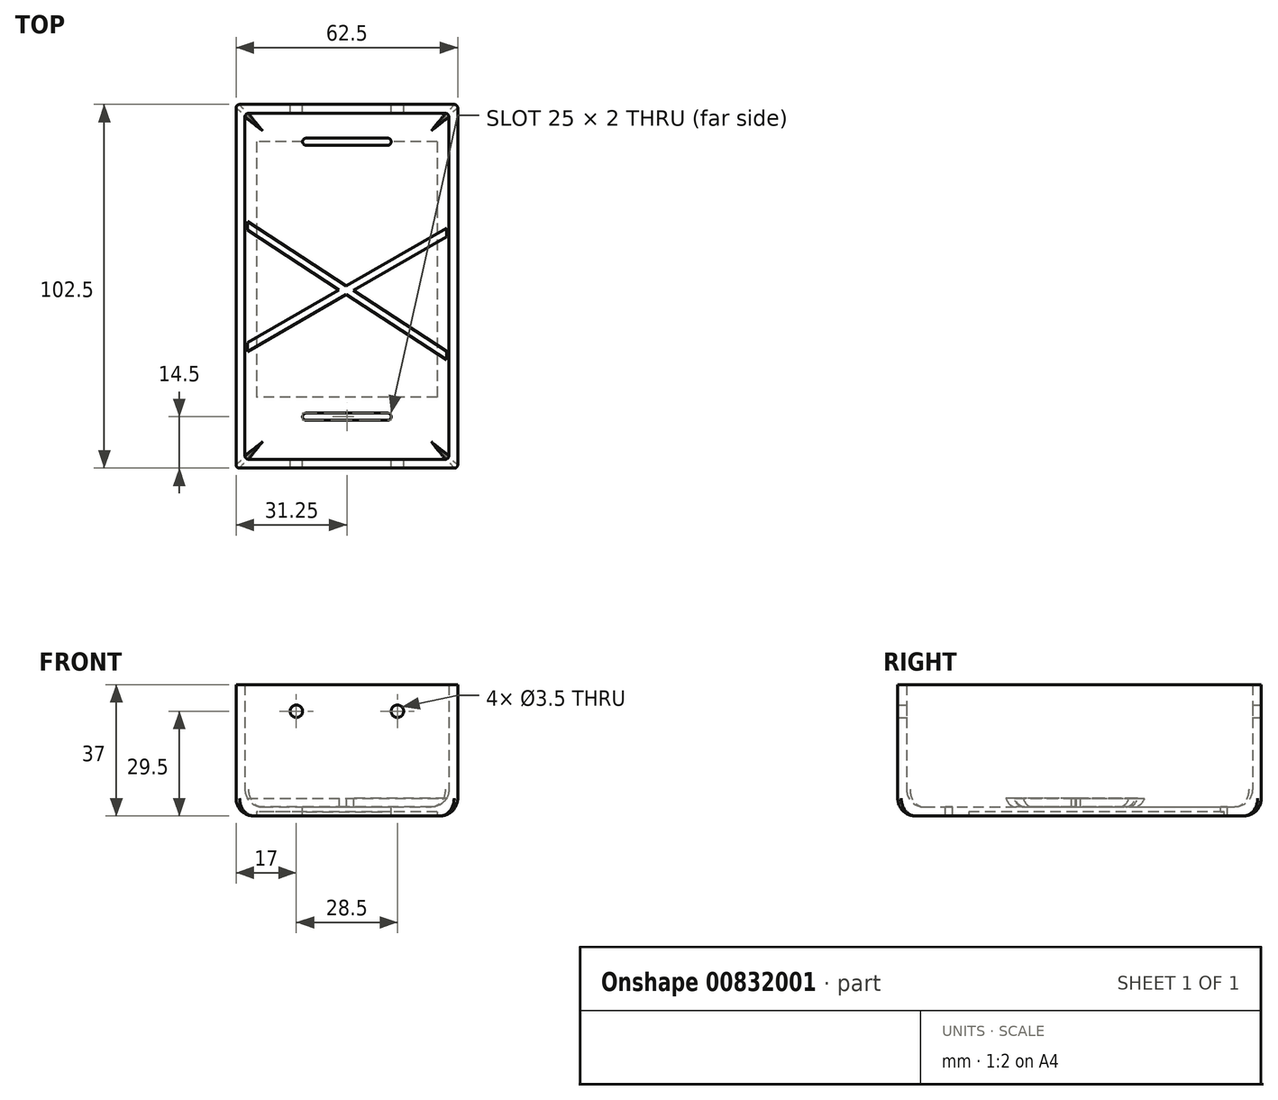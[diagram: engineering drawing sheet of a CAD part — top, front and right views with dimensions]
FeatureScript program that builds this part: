
annotation { "Feature Type Name" : "Feature", "Feature Type Description" : "" }
export const myFeature = defineFeature(function(context is Context, id is Id, definition is map)
    precondition{}
    {
        {
            assignVariable(context, id + "F0", {"name" : "d", "anyValue" : 2.5});
        }
        {
            var Q0;
            Q0=qCreatedBy(makeId("Top.planeOp"),FACE);
            var sketch = newSketch(context, id + "F1", { "sketchPlane" : qUnion([Q0])});
            skLineSegment(sketch, "E0.bottom", {"start": v(0, 0) * mm, "end": v(57.5, 0) * mm});
            skLineSegment(sketch, "E0.top", {"start": v(0, 97.5) * mm, "end": v(57.5, 97.5) * mm});
            skLineSegment(sketch, "E0.left", {"start": v(0, 0) * mm, "end": v(0, 97.5) * mm});
            skLineSegment(sketch, "E0.right", {"start": v(57.5, 0) * mm, "end": v(57.5, 97.5) * mm});
            skLineSegment(sketch, "E1.0", {"start": v(-2.5, 100) * mm, "end": v(60, 100) * mm});
            skLineSegment(sketch, "E1.1", {"start": v(-2.5, -2.5) * mm, "end": v(-2.5, 100) * mm});
            skLineSegment(sketch, "E1.2", {"start": v(-2.5, -2.5) * mm, "end": v(60, -2.5) * mm});
            skLineSegment(sketch, "E1.3", {"start": v(60, -2.5) * mm, "end": v(60, 100) * mm});
            skSolve(sketch);
        }
        {
            var Q0;
            Q0 = qSketchRegion(id + "F1", true);
            extrude(context, id + "F2", {"entities" : qUnion([Q0]), "depth" : 37 * mm, "offsetDistance" : 25 * mm});
        }
        {
            var Q0;
            Q0=qCreatedBy(makeId("Top.planeOp"),FACE);
            var sketch = newSketch(context, id + "F3", { "sketchPlane" : qUnion([Q0])});
            skLineSegment(sketch, "E2.bottom", {"start": v(60, 100) * mm, "end": v(-2.5, 100) * mm});
            skLineSegment(sketch, "E2.top", {"start": v(60, -2.5) * mm, "end": v(-2.5, -2.5) * mm});
            skLineSegment(sketch, "E2.left", {"start": v(60, 100) * mm, "end": v(60, -2.5) * mm});
            skLineSegment(sketch, "E2.right", {"start": v(-2.5, 100) * mm, "end": v(-2.5, -2.5) * mm});
            skSolve(sketch);
        }
        {
            var Q0;
            Q0 = qSketchRegion(id + "F3", true);
            extrude(context, id + "F4", {"entities" : qUnion([Q0]), "operationType" : NewBodyOperationType.ADD, "depth" : (getVariable(context, 'd')) * mm, "offsetDistance" : 25 * mm});
        }
        {
            var Q0;
            Q0=makeQuery(id+"F4.opExtrude","CAP_FACE",FACE,{"disambiguationData":[OSD([sQuery(id+"F3.wireOp",EDGE,"E2.bottom"),sQuery(id+"F3.wireOp",EDGE,"E2.top"),sQuery(id+"F3.wireOp",EDGE,"E2.left"),sQuery(id+"F3.wireOp",EDGE,"E2.right")])],"isStart":false});
            var sketch = newSketch(context, id + "F5", { "sketchPlane" : qUnion([Q0])});
            skLineSegment(sketch, "E3", {"start": v(17.25, 12) * mm, "end": v(40.25, 12) * mm});
            skLineSegment(sketch, "E4", {"start": v(17.25, 89.5) * mm, "end": v(40.25, 89.5) * mm});
            skPoint(sketch, "E5", {"position": v(28.75, 12) * mm});
            skPoint(sketch, "E6", {"position": v(28.75, 0) * mm});
            skArc(sketch, "E7.0.startCap", {"start": v(17.25, 88.5) * mm, "mid": v(16.25, 89.5) * mm, "end": v(17.25, 90.5) * mm});
            skArc(sketch, "E7.0.endCap", {"start": v(40.25, 90.5) * mm, "mid": v(41.25, 89.5) * mm, "end": v(40.25, 88.5) * mm});
            skLineSegment(sketch, "E7.0.left", {"start": v(17.25, 90.5) * mm, "end": v(40.25, 90.5) * mm});
            skLineSegment(sketch, "E7.0.right", {"start": v(17.25, 88.5) * mm, "end": v(40.25, 88.5) * mm});
            skArc(sketch, "E7.1.startCap", {"start": v(17.25, 11) * mm, "mid": v(16.25, 12) * mm, "end": v(17.25, 13) * mm});
            skArc(sketch, "E7.1.endCap", {"start": v(40.25, 13) * mm, "mid": v(41.25, 12) * mm, "end": v(40.25, 11) * mm});
            skLineSegment(sketch, "E7.1.left", {"start": v(17.25, 13) * mm, "end": v(40.25, 13) * mm});
            skLineSegment(sketch, "E7.1.right", {"start": v(17.25, 11) * mm, "end": v(40.25, 11) * mm});
            skSolve(sketch);
        }
        {
            var Q0;
            Q0 = qSketchRegion(id + "F5", true);
            extrude(context, id + "F6", {"entities" : qUnion([Q0]), "operationType" : NewBodyOperationType.REMOVE, "endBound" : BoundingType.THROUGH_ALL, "oppositeDirection" : true, "depth" : 25 * mm, "offsetDistance" : 25 * mm});
        }
        {
            var Q0;
            Q0=makeQuery(id+"F4.boolean.opBoolean","MERGE",FACE,{"derivedFrom":[makeQuery(id+"F2.opExtrude","CAP_FACE",FACE,{"disambiguationData":[OSD([sQuery(id+"F1.wireOp",EDGE,"E0.bottom"),sQuery(id+"F1.wireOp",EDGE,"E0.top"),sQuery(id+"F1.wireOp",EDGE,"E0.left"),sQuery(id+"F1.wireOp",EDGE,"E0.right"),sQuery(id+"F1.wireOp",EDGE,"E1.0"),sQuery(id+"F1.wireOp",EDGE,"E1.1"),sQuery(id+"F1.wireOp",EDGE,"E1.2"),sQuery(id+"F1.wireOp",EDGE,"E1.3")])],"isStart":true}),makeQuery(id+"F4.opExtrude","CAP_FACE",FACE,{"disambiguationData":[OSD([sQuery(id+"F3.wireOp",EDGE,"E2.bottom"),sQuery(id+"F3.wireOp",EDGE,"E2.top"),sQuery(id+"F3.wireOp",EDGE,"E2.left"),sQuery(id+"F3.wireOp",EDGE,"E2.right")])],"isStart":true})]});
            var sketch = newSketch(context, id + "F7", { "sketchPlane" : qUnion([Q0])});
            skLineSegment(sketch, "E8.bottom", {"start": v(54.25, -89.5) * mm, "end": v(3.25, -89.5) * mm});
            skLineSegment(sketch, "E8.top", {"start": v(54.25, -17.5) * mm, "end": v(3.25, -17.5) * mm});
            skLineSegment(sketch, "E8.left", {"start": v(54.25, -89.5) * mm, "end": v(54.25, -17.5) * mm});
            skLineSegment(sketch, "E8.right", {"start": v(3.25, -89.5) * mm, "end": v(3.25, -17.5) * mm});
            skPoint(sketch, "E9", {"position": v(28.75, -100) * mm});
            skPoint(sketch, "E10", {"position": v(28.75, -89.5) * mm});
            skSolve(sketch);
        }
        {
            var Q0;
            Q0 = qSketchRegion(id + "F7", true);
            extrude(context, id + "F8", {"entities" : qUnion([Q0]), "operationType" : NewBodyOperationType.REMOVE, "oppositeDirection" : true, "depth" : 1.2 * mm, "offsetDistance" : 25 * mm});
        }
        {
            var Q0;
            Q0=makeQuery(id+"F4.opExtrude","CAP_FACE",FACE,{"disambiguationData":[OSD([sQuery(id+"F3.wireOp",EDGE,"E2.bottom"),sQuery(id+"F3.wireOp",EDGE,"E2.top"),sQuery(id+"F3.wireOp",EDGE,"E2.left"),sQuery(id+"F3.wireOp",EDGE,"E2.right")])],"isStart":false});
            var sketch = newSketch(context, id + "F9", { "sketchPlane" : qUnion([Q0])});
            skLineSegment(sketch, "E11", {"start": v(0, 30) * mm, "end": v(57.5, 63.04) * mm});
            skLineSegment(sketch, "E12", {"start": v(57.5, 63.04) * mm, "end": v(57.5, 65.54) * mm});
            skLineSegment(sketch, "E13", {"start": v(57.5, 65.54) * mm, "end": v(0, 32.5) * mm});
            skLineSegment(sketch, "E14", {"start": v(0, 32.5) * mm, "end": v(0, 30) * mm});
            skLineSegment(sketch, "E15", {"start": v(0, 65) * mm, "end": v(57.5, 27.58) * mm});
            skLineSegment(sketch, "E16", {"start": v(57.5, 27.58) * mm, "end": v(57.5, 30.08) * mm});
            skLineSegment(sketch, "E17", {"start": v(57.5, 30.08) * mm, "end": v(0, 67.5) * mm});
            skLineSegment(sketch, "E18", {"start": v(0, 67.5) * mm, "end": v(0, 65) * mm});
            skSolve(sketch);
        }
        {
            var Q0;
            Q0 = qSketchRegion(id + "F9", true);
            extrude(context, id + "F10", {"entities" : qUnion([Q0]), "operationType" : NewBodyOperationType.ADD, "depth" : (getVariable(context, 'd')) * mm, "offsetDistance" : 25 * mm});
        }
        {
            var Q0;
            Q0=makeQuery(id+"F2.opExtrude","SWEPT_FACE",FACE,{"disambiguationData":[OSD([sQuery(id+"F1.wireOp",EDGE,"E1.0")])]});
            var sketch = newSketch(context, id + "F11", { "sketchPlane" : qUnion([Q0])});
            skLineSegment(sketch, "E19", {"start": v(14.05, 29.5) * mm, "end": v(-65.83, 29.5) * mm, "construction": true});
            skCircle(sketch, "E20", {"center": v(-14.5, 29.5) * mm, "radius": 1.75 * mm});
            skCircle(sketch, "E21", {"center": v(-43, 29.5) * mm, "radius": 1.75 * mm});
            skSolve(sketch);
        }
        {
            var Q0;
            Q0 = qSketchRegion(id + "F11", true);
            extrude(context, id + "F12", {"entities" : qUnion([Q0]), "operationType" : NewBodyOperationType.REMOVE, "endBound" : BoundingType.THROUGH_ALL, "oppositeDirection" : true, "depth" : (getVariable(context, 'd')) * mm, "offsetDistance" : 25 * mm});
        }
        {
            var Q0;
            Q0=makeQuery(id+"F2.opExtrude","CAP_EDGE",EDGE,{"disambiguationData":[OSD([sQuery(id+"F1.wireOp",EDGE,"E1.1")])],"isStart":true});
            var Q1;
            Q1=makeQuery(id+"F2.opExtrude","CAP_EDGE",EDGE,{"disambiguationData":[OSD([sQuery(id+"F1.wireOp",EDGE,"E1.0")])],"isStart":true});
            var Q2;
            Q2=makeQuery(id+"F2.opExtrude","CAP_EDGE",EDGE,{"disambiguationData":[OSD([sQuery(id+"F1.wireOp",EDGE,"E1.2")])],"isStart":true});
            var Q3;
            Q3=makeQuery(id+"F2.opExtrude","CAP_EDGE",EDGE,{"disambiguationData":[OSD([sQuery(id+"F1.wireOp",EDGE,"E1.3")])],"isStart":true});
            var Q4;
            Q4=makeQuery(id+"F4.boolean.opBoolean","INTERSECT",EDGE,{"derivedFrom":[makeQuery(id+"F2.opExtrude","SWEPT_FACE",FACE,{"disambiguationData":[OSD([sQuery(id+"F1.wireOp",EDGE,"E0.left")])]}),makeQuery(id+"F4.opExtrude","CAP_FACE",FACE,{"disambiguationData":[OSD([sQuery(id+"F3.wireOp",EDGE,"E2.bottom"),sQuery(id+"F3.wireOp",EDGE,"E2.top"),sQuery(id+"F3.wireOp",EDGE,"E2.left"),sQuery(id+"F3.wireOp",EDGE,"E2.right")])],"isStart":false})]});
            var Q5;
            Q5=makeQuery(id+"F4.boolean.opBoolean","INTERSECT",EDGE,{"derivedFrom":[makeQuery(id+"F2.opExtrude","SWEPT_FACE",FACE,{"disambiguationData":[OSD([sQuery(id+"F1.wireOp",EDGE,"E0.bottom")])]}),makeQuery(id+"F4.opExtrude","CAP_FACE",FACE,{"disambiguationData":[OSD([sQuery(id+"F3.wireOp",EDGE,"E2.bottom"),sQuery(id+"F3.wireOp",EDGE,"E2.top"),sQuery(id+"F3.wireOp",EDGE,"E2.left"),sQuery(id+"F3.wireOp",EDGE,"E2.right")])],"isStart":false})]});
            var Q6;
            Q6=makeQuery(id+"F4.boolean.opBoolean","INTERSECT",EDGE,{"derivedFrom":[makeQuery(id+"F2.opExtrude","SWEPT_FACE",FACE,{"disambiguationData":[OSD([sQuery(id+"F1.wireOp",EDGE,"E0.right")])]}),makeQuery(id+"F4.opExtrude","CAP_FACE",FACE,{"disambiguationData":[OSD([sQuery(id+"F3.wireOp",EDGE,"E2.bottom"),sQuery(id+"F3.wireOp",EDGE,"E2.top"),sQuery(id+"F3.wireOp",EDGE,"E2.left"),sQuery(id+"F3.wireOp",EDGE,"E2.right")])],"isStart":false})]});
            var Q7;
            Q7=makeQuery(id+"F4.boolean.opBoolean","INTERSECT",EDGE,{"derivedFrom":[makeQuery(id+"F2.opExtrude","SWEPT_FACE",FACE,{"disambiguationData":[OSD([sQuery(id+"F1.wireOp",EDGE,"E0.top")])]}),makeQuery(id+"F4.opExtrude","CAP_FACE",FACE,{"disambiguationData":[OSD([sQuery(id+"F3.wireOp",EDGE,"E2.bottom"),sQuery(id+"F3.wireOp",EDGE,"E2.top"),sQuery(id+"F3.wireOp",EDGE,"E2.left"),sQuery(id+"F3.wireOp",EDGE,"E2.right")])],"isStart":false})]});
            fillet(context, id + "F13", {"entities" : qUnion([Q0, Q1, Q2, Q3, Q4, Q5, Q6, Q7]), "radius" : 5 * mm, "tangentPropagation" : true, "allowEdgeOverflow" : false});
        }
        {
            var Q0;
            Q0=makeQuery(id+"F2.opExtrude","SWEPT_EDGE",EDGE,{"disambiguationData":[OSD([sQuery(id+"F1.wireOp",EDGE,"E1.0"),sQuery(id+"F1.wireOp",EDGE,"E1.3")])]});
            var Q1;
            Q1=makeQuery(id+"F2.opExtrude","SWEPT_EDGE",EDGE,{"disambiguationData":[OSD([sQuery(id+"F1.wireOp",EDGE,"E1.0"),sQuery(id+"F1.wireOp",EDGE,"E1.1")])]});
            var Q2;
            Q2=makeQuery(id+"F2.opExtrude","SWEPT_EDGE",EDGE,{"disambiguationData":[OSD([sQuery(id+"F1.wireOp",EDGE,"E1.1"),sQuery(id+"F1.wireOp",EDGE,"E1.2")])]});
            var Q3;
            Q3=makeQuery(id+"F2.opExtrude","SWEPT_EDGE",EDGE,{"disambiguationData":[OSD([sQuery(id+"F1.wireOp",EDGE,"E1.2"),sQuery(id+"F1.wireOp",EDGE,"E1.3")])]});
            var Q4;
            Q4=makeQuery(id+"F2.opExtrude","SWEPT_EDGE",EDGE,{"disambiguationData":[OSD([sQuery(id+"F1.wireOp",EDGE,"E0.bottom"),sQuery(id+"F1.wireOp",EDGE,"E0.left")])]});
            var Q5;
            Q5=makeQuery(id+"F2.opExtrude","SWEPT_EDGE",EDGE,{"disambiguationData":[OSD([sQuery(id+"F1.wireOp",EDGE,"E0.bottom"),sQuery(id+"F1.wireOp",EDGE,"E0.right")])]});
            var Q6;
            Q6=makeQuery(id+"F2.opExtrude","SWEPT_EDGE",EDGE,{"disambiguationData":[OSD([sQuery(id+"F1.wireOp",EDGE,"E0.top"),sQuery(id+"F1.wireOp",EDGE,"E0.right")])]});
            var Q7;
            Q7=makeQuery(id+"F2.opExtrude","SWEPT_EDGE",EDGE,{"disambiguationData":[OSD([sQuery(id+"F1.wireOp",EDGE,"E0.top"),sQuery(id+"F1.wireOp",EDGE,"E0.left")])]});
            fillet(context, id + "F14", {"entities" : qUnion([Q0, Q1, Q2, Q3, Q4, Q5, Q6, Q7]), "radius" : 1 * mm, "tangentPropagation" : true, "allowEdgeOverflow" : false});
        }
    });
